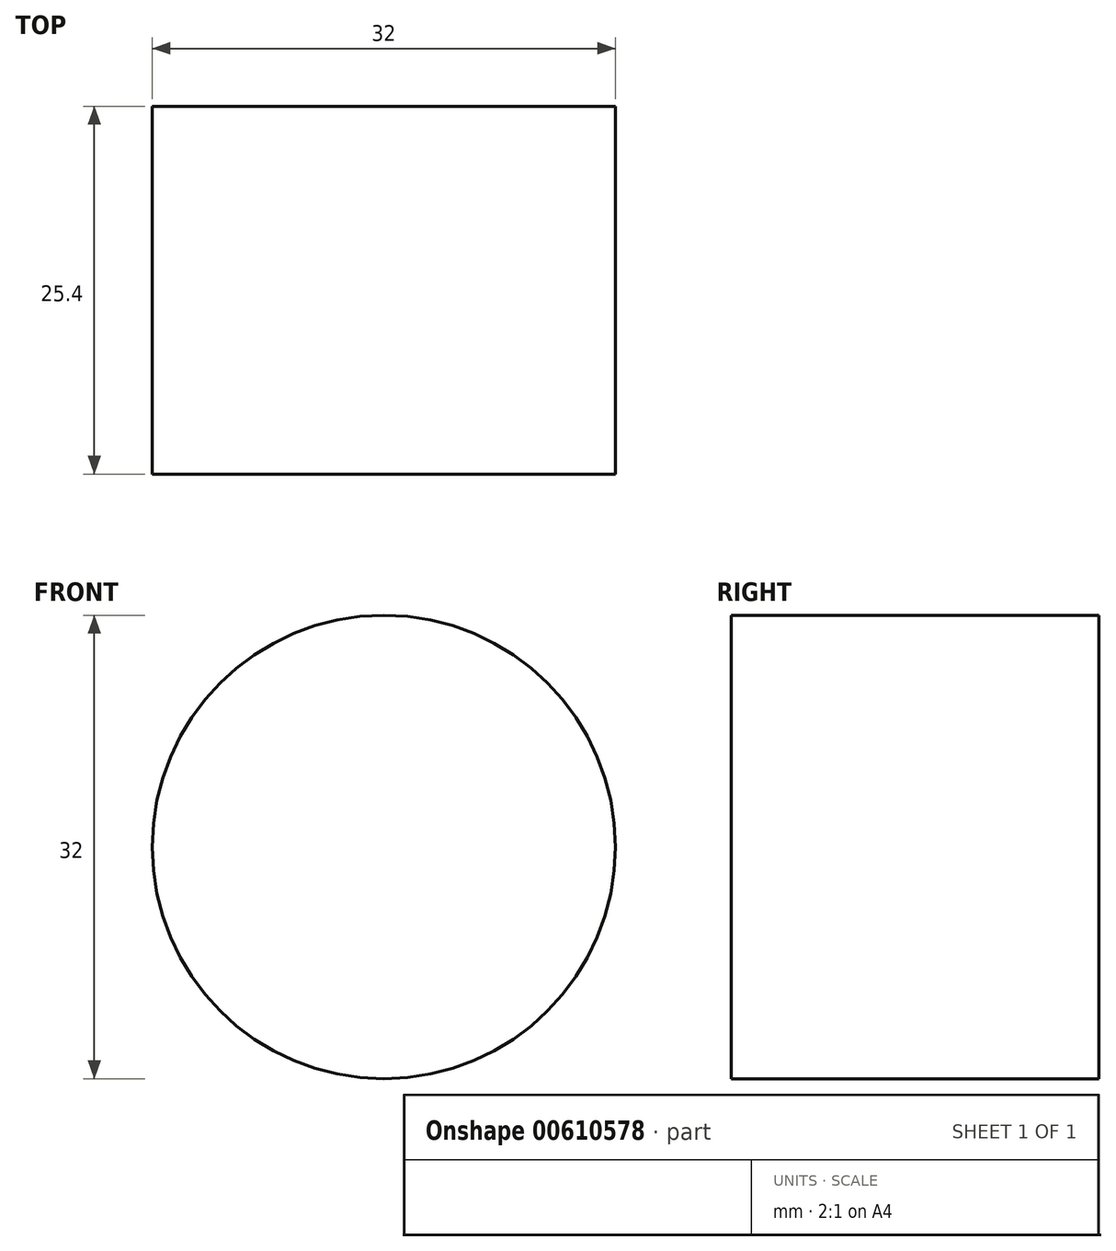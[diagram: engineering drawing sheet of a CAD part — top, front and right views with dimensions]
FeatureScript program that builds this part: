
annotation { "Feature Type Name" : "Feature", "Feature Type Description" : "" }
export const myFeature = defineFeature(function(context is Context, id is Id, definition is map)
    precondition{}
    {
        {
            var Q0;
            Q0=qCreatedBy(makeId("Front.planeOp"),FACE);
            var sketch = newSketch(context, id + "F0", { "sketchPlane" : qUnion([Q0])});
            skCircle(sketch, "E0", {"center": v(0, 0) * mm, "radius": 16 * mm});
            skSolve(sketch);
        }
        {
            var Q0;
            Q0 = qSketchRegion(id + "F0", true);
            extrude(context, id + "F1", {"entities" : qUnion([Q0]), "depth" : 25.4 * mm, "offsetDistance" : 25.4 * mm});
        }
    });
